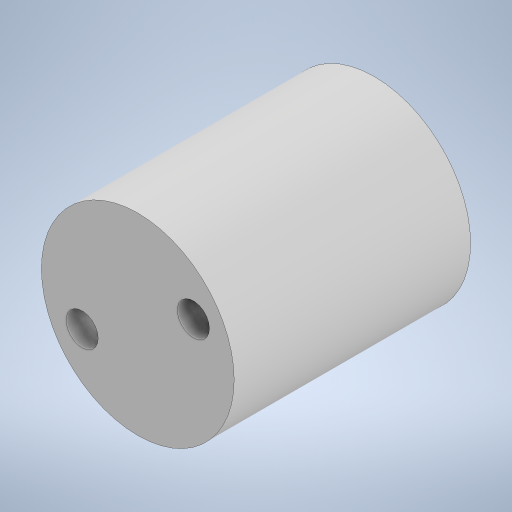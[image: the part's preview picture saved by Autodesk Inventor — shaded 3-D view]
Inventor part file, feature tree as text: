
AUTODESK INVENTOR PART (.ipt)
format: ipt  version: 2023 (Build 270158000, 158)  size: 223,744 bytes
history: native  units: in
note: dims shown in document units (in); Inventor stores cm internally (conversion verified against a paired STEP export)
features: extrude x3, sketch x2
ambient origin geometry x8: Origin, YZ Plane, XZ Plane, XY Plane, X Axis, Y Axis, Z Axis, Center Point
bodies: Body1 (feature_tree)
feature tree (5):
  sketch  "Sketch1"  dims[d3=0.125in d4=0.125in]
  extrude  "Extrusion2"  Depth=0.125in
  extrude  "Extrusion3"  Depth=0.25in TaperAngle=0.0deg
  extrude  "Extrusion4"  Depth=0.25in
  sketch  "Sketch2"  dims[d12=0.92in d13=0.0in d14=0.25in d15=0.0in d22=0.25in d23=0.5in d24=0.125in d25=0.125in d26=0.25in d27=0.0in]
